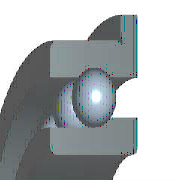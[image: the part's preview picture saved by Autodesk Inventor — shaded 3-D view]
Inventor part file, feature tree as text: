
AUTODESK INVENTOR PART (.ipt)
format: ipt  version: 2020 (Build 240168000, 168)  size: 335,872 bytes
history: native  units: mm (DEFAULTED — no unit token found)
features: other x1, pattern_circular x1
ambient origin geometry x8: Origin, YZ Plane, XZ Plane, XY Plane, X Axis, Y Axis, Z Axis, Center Point
bodies: Solid1 (feature_tree), Body (feature_tree)
feature tree (2):
  other  "Ball"
  pattern_circular  "Balls"  [2 undecoded]
note: 2 required parameter values undecoded (feature->parameter linkage not recoverable at this tier; creation-order binding heuristic only, values carry confidence <= 0.55)
